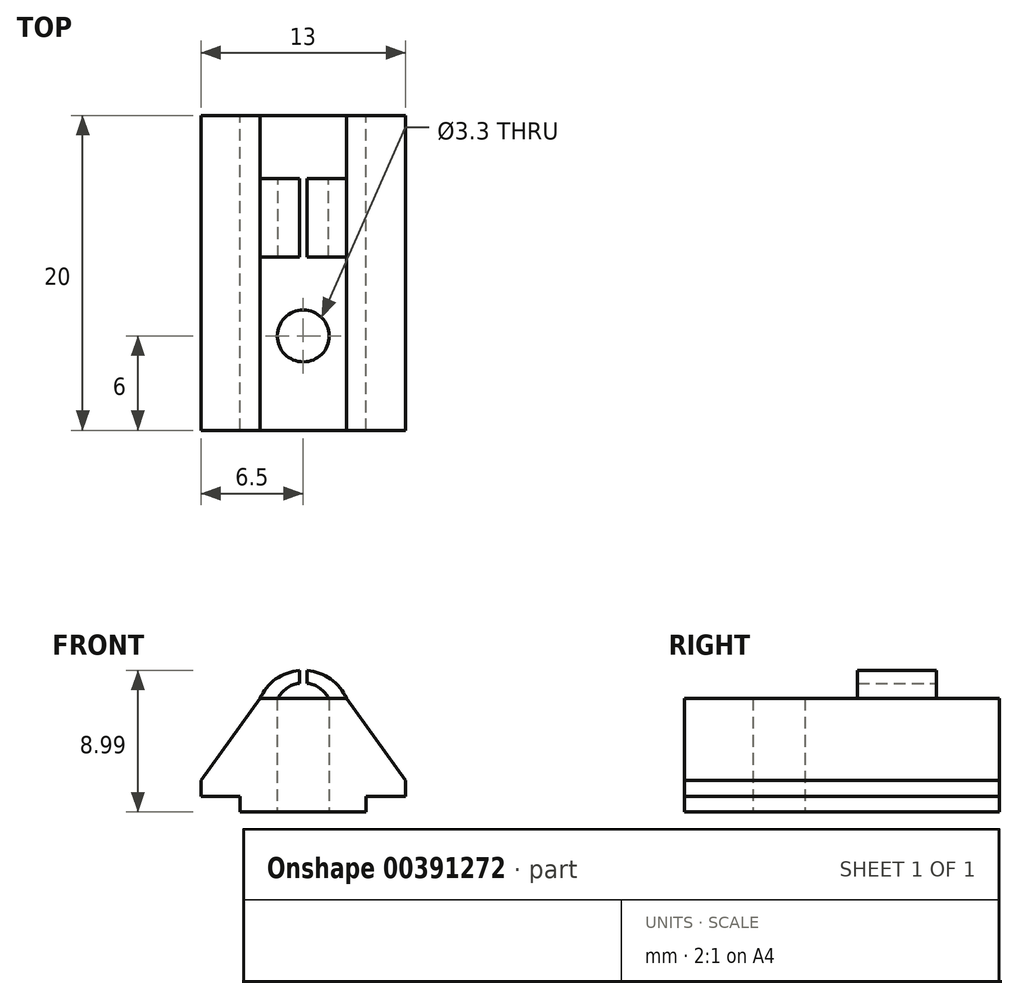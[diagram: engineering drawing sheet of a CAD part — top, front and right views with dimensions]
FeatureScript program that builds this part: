
annotation { "Feature Type Name" : "Feature", "Feature Type Description" : "" }
export const myFeature = defineFeature(function(context is Context, id is Id, definition is map)
    precondition{}
    {
        {
            var Q0;
            Q0=qCreatedBy(makeId("Front.planeOp"),FACE);
            var sketch = newSketch(context, id + "F0", { "sketchPlane" : qUnion([Q0])});
            skLineSegment(sketch, "E0", {"start": v(0, 0) * mm, "end": v(4, 0) * mm});
            skLineSegment(sketch, "E1", {"start": v(4, 0) * mm, "end": v(4, 1) * mm});
            skLineSegment(sketch, "E2", {"start": v(4, 1) * mm, "end": v(6.5, 1) * mm});
            skLineSegment(sketch, "E3", {"start": v(6.5, 1) * mm, "end": v(6.5, 2) * mm});
            skLineSegment(sketch, "E4", {"start": v(6.5, 2) * mm, "end": v(2.75, 7.2) * mm});
            skLineSegment(sketch, "E5", {"start": v(2.75, 7.2) * mm, "end": v(0, 7.2) * mm});
            skLineSegment(sketch, "E6.MirrorCS", {"start": v(-2.75, 7.2) * mm, "end": v(0, 7.2) * mm});
            skLineSegment(sketch, "E7.MirrorCS", {"start": v(0, 0) * mm, "end": v(-4, 0) * mm});
            skLineSegment(sketch, "E8.MirrorCS", {"start": v(-6.5, 2) * mm, "end": v(-2.75, 7.2) * mm});
            skLineSegment(sketch, "E9.MirrorCS", {"start": v(-4, 1) * mm, "end": v(-6.5, 1) * mm});
            skLineSegment(sketch, "E10.MirrorCS", {"start": v(-6.5, 1) * mm, "end": v(-6.5, 2) * mm});
            skLineSegment(sketch, "E11.MirrorCS", {"start": v(-4, 0) * mm, "end": v(-4, 1) * mm});
            skSolve(sketch);
        }
        {
            var Q0;
            Q0=makeQuery(id+"F0.imprint","IMPRINT",FACE,{"disambiguationData":[TD([[makeQuery(id+"F0.imprint","IMPRINT",EDGE,{"derivedFrom":sQuery(id+"F0.wireOp",EDGE,"E0")}),1.0]])]});
            extrude(context, id + "F1", {"entities" : qUnion([Q0]), "depth" : 20 * mm});
        }
        {
            var Q0;
            Q0=makeQuery(id+"F1.opExtrude","SWEPT_FACE",FACE,{"disambiguationData":[OSD([sQuery(id+"F0.wireOp",EDGE,"E0"),sQuery(id+"F0.wireOp",EDGE,"E7.MirrorCS")])]});
            var sketch = newSketch(context, id + "F2", { "sketchPlane" : qUnion([Q0])});
            skCircle(sketch, "E12", {"center": v(0, 14) * mm, "radius": 1.65 * mm});
            skSolve(sketch);
        }
        {
            var Q0;
            Q0=makeQuery(id+"F2.imprint","IMPRINT",FACE,{"disambiguationData":[TD([[makeQuery(id+"F2.imprint","IMPRINT",EDGE,{"derivedFrom":sQuery(id+"F2.wireOp",EDGE,"E12")}),1.0]])]});
            extrude(context, id + "F3", {"entities" : qUnion([Q0]), "operationType" : NewBodyOperationType.REMOVE, "endBound" : BoundingType.THROUGH_ALL, "oppositeDirection" : true, "depth" : 25 * mm});
        }
        {
            var Q0;
            Q0=qCreatedBy(makeId("Front.planeOp"),FACE);
            var sketch = newSketch(context, id + "F4", { "sketchPlane" : qUnion([Q0])});
            skArc(sketch, "E13", {"start": v(2.75, 7.2) * mm, "mid": v(0, 9) * mm, "end": v(-2.75, 7.2) * mm});
            skArc(sketch, "E14.0", {"start": v(1.61, 7.2) * mm, "mid": v(0, 8.2) * mm, "end": v(-1.61, 7.2) * mm});
            skLineSegment(sketch, "E15", {"start": v(2.75, 7.2) * mm, "end": v(1.61, 7.2) * mm});
            skLineSegment(sketch, "E16", {"start": v(-2.75, 7.2) * mm, "end": v(-1.61, 7.2) * mm});
            skSolve(sketch);
        }
        {
            var Q0;
            Q0=makeQuery(id+"F4.imprint","IMPRINT",FACE,{"disambiguationData":[TD([[makeQuery(id+"F4.imprint","IMPRINT",EDGE,{"derivedFrom":sQuery(id+"F4.wireOp",EDGE,"E13")}),1.0]])]});
            extrude(context, id + "F5", {"entities" : qUnion([Q0]), "operationType" : NewBodyOperationType.ADD, "depth" : 9 * mm});
        }
        {
            var Q0;
            Q0=makeQuery(id+"F5.boolean.opBoolean","MERGE",FACE,{"derivedFrom":[makeQuery(id+"F1.opExtrude","CAP_FACE",FACE,{"disambiguationData":[OSD([sQuery(id+"F0.wireOp",EDGE,"E0"),sQuery(id+"F0.wireOp",EDGE,"E1"),sQuery(id+"F0.wireOp",EDGE,"E2"),sQuery(id+"F0.wireOp",EDGE,"E3"),sQuery(id+"F0.wireOp",EDGE,"E4"),sQuery(id+"F0.wireOp",EDGE,"E5"),sQuery(id+"F0.wireOp",EDGE,"E6.MirrorCS"),sQuery(id+"F0.wireOp",EDGE,"E7.MirrorCS"),sQuery(id+"F0.wireOp",EDGE,"E8.MirrorCS"),sQuery(id+"F0.wireOp",EDGE,"E9.MirrorCS"),sQuery(id+"F0.wireOp",EDGE,"E10.MirrorCS"),sQuery(id+"F0.wireOp",EDGE,"E11.MirrorCS")])],"isStart":true}),makeQuery(id+"F5.opExtrude","CAP_FACE",FACE,{"disambiguationData":[OSD([sQuery(id+"F4.wireOp",EDGE,"E13"),sQuery(id+"F4.wireOp",EDGE,"E14.0"),sQuery(id+"F4.wireOp",EDGE,"E15"),sQuery(id+"F4.wireOp",EDGE,"E16")])],"isStart":true})]});
            var sketch = newSketch(context, id + "F6", { "sketchPlane" : qUnion([Q0])});
            skLineSegment(sketch, "E17.bottom", {"start": v(-2.75, 7.2) * mm, "end": v(2.75, 7.2) * mm});
            skLineSegment(sketch, "E17.top", {"start": v(-2.75, 9.86) * mm, "end": v(2.75, 9.86) * mm});
            skLineSegment(sketch, "E17.left", {"start": v(-2.75, 7.2) * mm, "end": v(-2.75, 9.86) * mm});
            skLineSegment(sketch, "E17.right", {"start": v(2.75, 7.2) * mm, "end": v(2.75, 9.86) * mm});
            skSolve(sketch);
        }
        {
            var Q0;
            {var subQ1=makeQuery(id+"F5.opExtrude","CAP_EDGE",EDGE,{"disambiguationData":[OSD([sQuery(id+"F4.wireOp",EDGE,"E13")])],"isStart":true});Q0=makeQuery(id+"F6.imprint","IMPRINT",FACE,{"disambiguationData":[TD([[makeQuery(id+"F6.imprint","IMPRINT",EDGE,{"derivedFrom":subQ1}),-1.0]])]});}
            extrude(context, id + "F7", {"entities" : qUnion([Q0]), "operationType" : NewBodyOperationType.REMOVE, "oppositeDirection" : true, "depth" : 4 * mm});
        }
        {
            var Q0;
            Q0=makeQuery(id+"F7.boolean.opBoolean","COPY",FACE,{"derivedFrom":makeQuery(id+"F7.opExtrude","CAP_FACE",FACE,{"disambiguationData":[OSD([sQuery(id+"F4.wireOp",EDGE,"E13"),sQuery(id+"F4.wireOp",EDGE,"E14.0"),sQuery(id+"F6.wireOp",EDGE,"E17.bottom")])],"isStart":false})});
            var sketch = newSketch(context, id + "F8", { "sketchPlane" : qUnion([Q0])});
            skLineSegment(sketch, "E18.bottom", {"start": v(-0.25, 7.86) * mm, "end": v(0.25, 7.86) * mm});
            skLineSegment(sketch, "E18.top", {"start": v(-0.25, 10.14) * mm, "end": v(0.25, 10.14) * mm});
            skLineSegment(sketch, "E18.left", {"start": v(-0.25, 7.86) * mm, "end": v(-0.25, 10.14) * mm});
            skLineSegment(sketch, "E18.right", {"start": v(0.25, 7.86) * mm, "end": v(0.25, 10.14) * mm});
            skPoint(sketch, "E18.middle", {"position": v(0, 9) * mm});
            skSolve(sketch);
        }
        {
            var Q0;
            {var subQ0=sQuery(id+"F8.wireOp",EDGE,"E18.left");var subQ1=makeQuery(id+"F7.boolean.opBoolean","COPY",EDGE,{"derivedFrom":makeQuery(id+"F7.opExtrude","CAP_EDGE",EDGE,{"disambiguationData":[OSD([sQuery(id+"F4.wireOp",EDGE,"E14.0")])],"isStart":false})});var subQ2=makeQuery(id+"F8.imprint","INTERSECT",VERTEX,{"derivedFrom":[subQ1,subQ0]});Q0=makeQuery(id+"F8.imprint","IMPRINT",FACE,{"disambiguationData":[TD([[makeQuery(id+"F8.imprint","IMPRINT",EDGE,{"disambiguationData":[TD([[subQ2,-1.0]])],"derivedFrom":subQ0}),-1.0]])]});}
            extrude(context, id + "F9", {"entities" : qUnion([Q0]), "operationType" : NewBodyOperationType.REMOVE, "endBound" : BoundingType.THROUGH_ALL, "oppositeDirection" : true, "depth" : 25 * mm});
        }
    });
